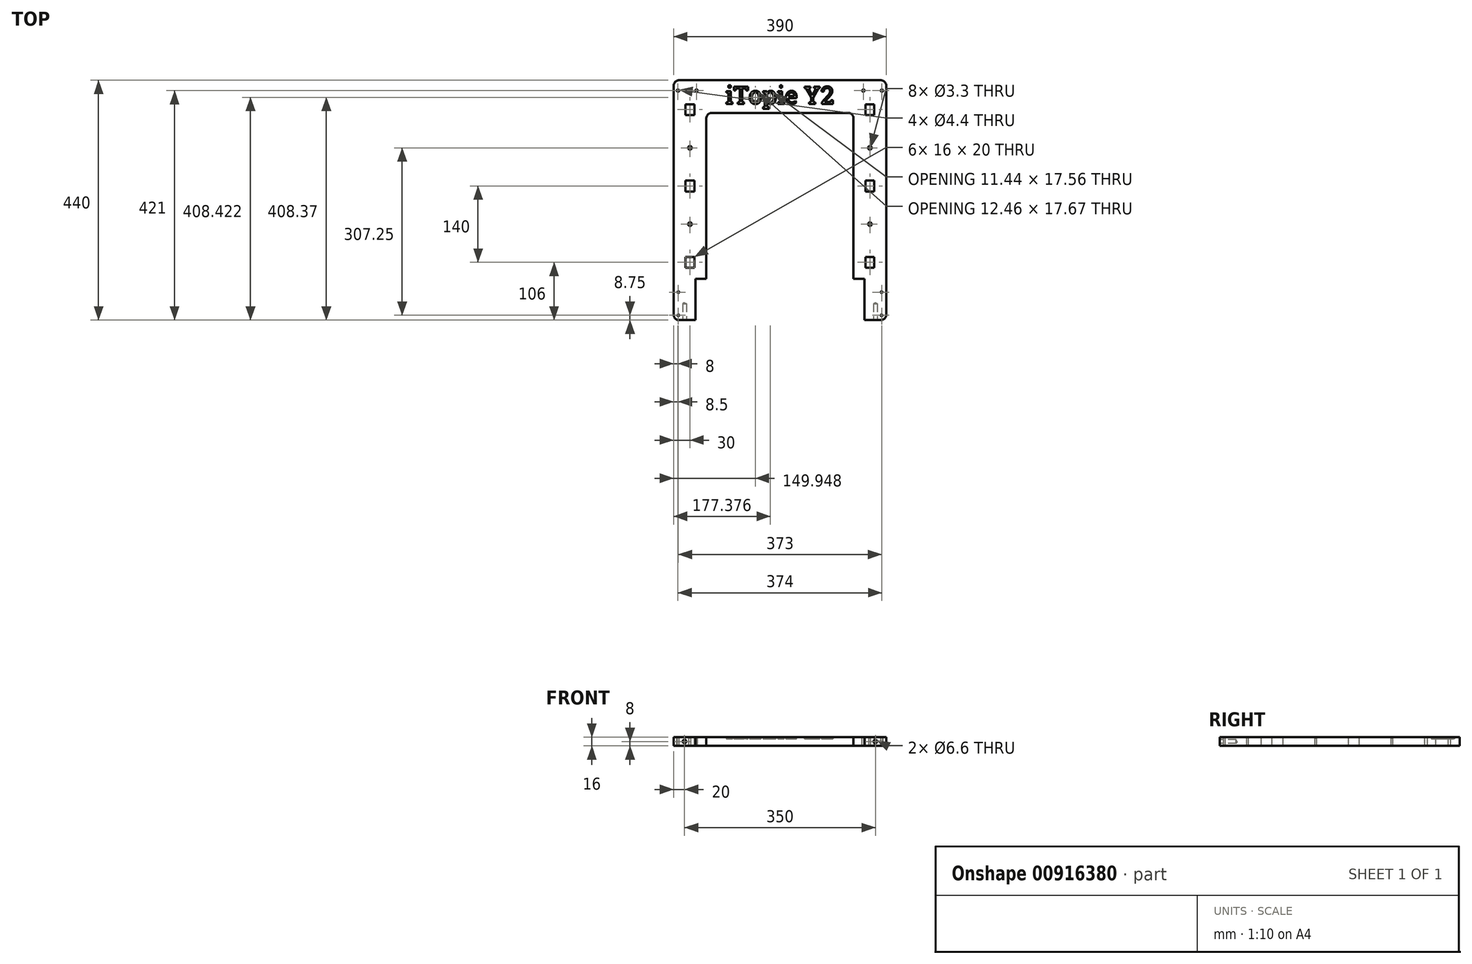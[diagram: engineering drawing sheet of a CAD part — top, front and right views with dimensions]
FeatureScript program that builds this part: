
annotation { "Feature Type Name" : "Feature", "Feature Type Description" : "" }
export const myFeature = defineFeature(function(context is Context, id is Id, definition is map)
    precondition{}
    {
        {
            var Q0;
            Q0=qCreatedBy(makeId("Top.planeOp"),FACE);
            var sketch = newSketch(context, id + "F0", { "sketchPlane" : qUnion([Q0])});
            skLineSegment(sketch, "E0.bottom", {"start": v(195, 220) * mm, "end": v(-195, 220) * mm});
            skLineSegment(sketch, "E0.top", {"start": v(195, -220) * mm, "end": v(-195, -220) * mm});
            skLineSegment(sketch, "E0.left", {"start": v(195, 220) * mm, "end": v(195, -220) * mm});
            skLineSegment(sketch, "E0.right", {"start": v(-195, 220) * mm, "end": v(-195, -220) * mm});
            skPoint(sketch, "E0.middle", {"position": v(0, 0) * mm});
            skLineSegment(sketch, "E1", {"start": v(-135, -220) * mm, "end": v(-135, 160) * mm});
            skLineSegment(sketch, "E2", {"start": v(-135, 160) * mm, "end": v(135, 160) * mm});
            skLineSegment(sketch, "E3", {"start": v(135, 160) * mm, "end": v(135, -220) * mm});
            skLineSegment(sketch, "E4", {"start": v(0, 0) * mm, "end": v(0, 160) * mm, "construction": true});
            skSolve(sketch);
        }
        {
            var Q0;
            Q0=makeQuery(id+"F0.imprint","IMPRINT",FACE,{"disambiguationData":[TD([[makeQuery(id+"F0.imprint","IMPRINT",EDGE,{"derivedFrom":sQuery(id+"F0.wireOp",EDGE,"E0.bottom")}),1.0]])]});
            extrude(context, id + "F1", {"entities" : qUnion([Q0]), "depth" : 16 * mm});
        }
        {
            var Q0;
            Q0=makeQuery(id+"F1.opExtrude","CAP_FACE",FACE,{"disambiguationData":[OSD([sQuery(id+"F0.wireOp",EDGE,"E0.bottom"),sQuery(id+"F0.wireOp",EDGE,"E0.top"),sQuery(id+"F0.wireOp",EDGE,"E0.left"),sQuery(id+"F0.wireOp",EDGE,"E0.right"),sQuery(id+"F0.wireOp",EDGE,"E1"),sQuery(id+"F0.wireOp",EDGE,"E2"),sQuery(id+"F0.wireOp",EDGE,"E3")])],"isStart":false});
            var sketch = newSketch(context, id + "F2", { "sketchPlane" : qUnion([Q0])});
            skLineSegment(sketch, "E5", {"start": v(-165, 166) * mm, "end": v(-165, 26) * mm, "construction": true});
            skLineSegment(sketch, "E6", {"start": v(-165, 26) * mm, "end": v(-165, -114) * mm, "construction": true});
            skLineSegment(sketch, "E7.bottom", {"start": v(-157, 176) * mm, "end": v(-173, 176) * mm});
            skLineSegment(sketch, "E7.top", {"start": v(-157, 156) * mm, "end": v(-173, 156) * mm});
            skLineSegment(sketch, "E7.left", {"start": v(-157, 176) * mm, "end": v(-157, 156) * mm});
            skLineSegment(sketch, "E7.right", {"start": v(-173, 176) * mm, "end": v(-173, 156) * mm});
            skPoint(sketch, "E7.middle", {"position": v(-165, 166) * mm});
            skLineSegment(sketch, "E8.bottom", {"start": v(-157, 36) * mm, "end": v(-173, 36) * mm});
            skLineSegment(sketch, "E8.top", {"start": v(-157, 16) * mm, "end": v(-173, 16) * mm});
            skLineSegment(sketch, "E8.left", {"start": v(-157, 36) * mm, "end": v(-157, 16) * mm});
            skLineSegment(sketch, "E8.right", {"start": v(-173, 36) * mm, "end": v(-173, 16) * mm});
            skPoint(sketch, "E8.middle", {"position": v(-165, 26) * mm});
            skLineSegment(sketch, "E9.bottom", {"start": v(-157, -104) * mm, "end": v(-173, -104) * mm});
            skLineSegment(sketch, "E9.top", {"start": v(-157, -124) * mm, "end": v(-173, -124) * mm});
            skLineSegment(sketch, "E9.left", {"start": v(-157, -104) * mm, "end": v(-157, -124) * mm});
            skLineSegment(sketch, "E9.right", {"start": v(-173, -104) * mm, "end": v(-173, -124) * mm});
            skPoint(sketch, "E9.middle", {"position": v(-165, -114) * mm});
            skLineSegment(sketch, "E10.MirrorCS", {"start": v(157, 36) * mm, "end": v(173, 36) * mm});
            skLineSegment(sketch, "E11.MirrorCS", {"start": v(173, 176) * mm, "end": v(173, 156) * mm});
            skLineSegment(sketch, "E12.MirrorCS", {"start": v(157, 156) * mm, "end": v(173, 156) * mm});
            skLineSegment(sketch, "E13.MirrorCS", {"start": v(157, 176) * mm, "end": v(173, 176) * mm});
            skLineSegment(sketch, "E14.MirrorCS", {"start": v(157, 16) * mm, "end": v(173, 16) * mm});
            skLineSegment(sketch, "E15.MirrorCS", {"start": v(157, 36) * mm, "end": v(157, 16) * mm});
            skLineSegment(sketch, "E16.MirrorCS", {"start": v(173, 36) * mm, "end": v(173, 16) * mm});
            skLineSegment(sketch, "E17.MirrorCS", {"start": v(157, -104) * mm, "end": v(173, -104) * mm});
            skLineSegment(sketch, "E18.MirrorCS", {"start": v(157, -124) * mm, "end": v(173, -124) * mm});
            skLineSegment(sketch, "E19.MirrorCS", {"start": v(173, -104) * mm, "end": v(173, -124) * mm});
            skLineSegment(sketch, "E20.MirrorCS", {"start": v(157, -104) * mm, "end": v(157, -124) * mm});
            skLineSegment(sketch, "E21.MirrorCS", {"start": v(157, 176) * mm, "end": v(157, 156) * mm});
            skLineSegment(sketch, "E22.MirrorCS", {"start": v(165, 166) * mm, "end": v(165, 26) * mm, "construction": true});
            skLineSegment(sketch, "E23.MirrorCS", {"start": v(165, 26) * mm, "end": v(165, -114) * mm, "construction": true});
            skPoint(sketch, "E24.MirrorP", {"position": v(165, 26) * mm});
            skPoint(sketch, "E25.MirrorP", {"position": v(165, 166) * mm});
            skPoint(sketch, "E26.MirrorP", {"position": v(165, -114) * mm});
            skLineSegment(sketch, "E27.bottom", {"start": v(-135, -220) * mm, "end": v(-155, -220) * mm});
            skLineSegment(sketch, "E27.top", {"start": v(-135, -144) * mm, "end": v(-155, -144) * mm});
            skLineSegment(sketch, "E27.left", {"start": v(-135, -220) * mm, "end": v(-135, -144) * mm});
            skLineSegment(sketch, "E27.right", {"start": v(-155, -220) * mm, "end": v(-155, -144) * mm});
            skLineSegment(sketch, "E28.MirrorCS", {"start": v(135, -144) * mm, "end": v(155, -144) * mm});
            skLineSegment(sketch, "E29.MirrorCS", {"start": v(135, -220) * mm, "end": v(155, -220) * mm});
            skLineSegment(sketch, "E30.MirrorCS", {"start": v(155, -220) * mm, "end": v(155, -144) * mm});
            skLineSegment(sketch, "E31.MirrorCS", {"start": v(135, -220) * mm, "end": v(135, -144) * mm});
            skSolve(sketch);
        }
        {
            var Q0;
            Q0=makeQuery(id+"F2.imprint","IMPRINT",FACE,{"disambiguationData":[TD([[makeQuery(id+"F2.imprint","IMPRINT",EDGE,{"derivedFrom":sQuery(id+"F2.wireOp",EDGE,"E27.bottom")}),-1.0]])]});
            var Q1;
            Q1=makeQuery(id+"F2.imprint","IMPRINT",FACE,{"disambiguationData":[TD([[makeQuery(id+"F2.imprint","IMPRINT",EDGE,{"derivedFrom":sQuery(id+"F2.wireOp",EDGE,"E7.bottom")}),1.0]])]});
            var Q2;
            Q2=makeQuery(id+"F2.imprint","IMPRINT",FACE,{"disambiguationData":[TD([[makeQuery(id+"F2.imprint","IMPRINT",EDGE,{"derivedFrom":sQuery(id+"F2.wireOp",EDGE,"E9.bottom")}),1.0]])]});
            var Q3;
            Q3=makeQuery(id+"F2.imprint","IMPRINT",FACE,{"disambiguationData":[TD([[makeQuery(id+"F2.imprint","IMPRINT",EDGE,{"derivedFrom":sQuery(id+"F2.wireOp",EDGE,"E8.bottom")}),1.0]])]});
            var Q4;
            Q4=makeQuery(id+"F2.imprint","IMPRINT",FACE,{"disambiguationData":[TD([[makeQuery(id+"F2.imprint","IMPRINT",EDGE,{"derivedFrom":sQuery(id+"F2.wireOp",EDGE,"E28.MirrorCS")}),-1.0]])]});
            var Q5;
            Q5=makeQuery(id+"F2.imprint","IMPRINT",FACE,{"disambiguationData":[TD([[makeQuery(id+"F2.imprint","IMPRINT",EDGE,{"derivedFrom":sQuery(id+"F2.wireOp",EDGE,"E10.MirrorCS")}),-1.0]])]});
            var Q6;
            Q6=makeQuery(id+"F2.imprint","IMPRINT",FACE,{"disambiguationData":[TD([[makeQuery(id+"F2.imprint","IMPRINT",EDGE,{"derivedFrom":sQuery(id+"F2.wireOp",EDGE,"E11.MirrorCS")}),-1.0]])]});
            var Q7;
            Q7=makeQuery(id+"F2.imprint","IMPRINT",FACE,{"disambiguationData":[TD([[makeQuery(id+"F2.imprint","IMPRINT",EDGE,{"derivedFrom":sQuery(id+"F2.wireOp",EDGE,"E17.MirrorCS")}),-1.0]])]});
            extrude(context, id + "F3", {"entities" : qUnion([Q0, Q1, Q2, Q3, Q4, Q5, Q6, Q7]), "operationType" : NewBodyOperationType.REMOVE, "endBound" : BoundingType.UP_TO_NEXT, "oppositeDirection" : true, "depth" : 25 * mm});
        }
        {
            var Q0;
            Q0=makeQuery(id+"F1.opExtrude","SWEPT_EDGE",EDGE,{"disambiguationData":[OSD([sQuery(id+"F0.wireOp",EDGE,"E1"),sQuery(id+"F0.wireOp",EDGE,"E2")])]});
            var Q1;
            Q1=makeQuery(id+"F1.opExtrude","SWEPT_EDGE",EDGE,{"disambiguationData":[OSD([sQuery(id+"F0.wireOp",EDGE,"E2"),sQuery(id+"F0.wireOp",EDGE,"E3")])]});
            var Q2;
            Q2=makeQuery(id+"F1.opExtrude","SWEPT_EDGE",EDGE,{"disambiguationData":[OSD([sQuery(id+"F0.wireOp",EDGE,"E0.bottom"),sQuery(id+"F0.wireOp",EDGE,"E0.right")])]});
            var Q3;
            Q3=makeQuery(id+"F1.opExtrude","SWEPT_EDGE",EDGE,{"disambiguationData":[OSD([sQuery(id+"F0.wireOp",EDGE,"E0.bottom"),sQuery(id+"F0.wireOp",EDGE,"E0.left")])]});
            var Q4;
            Q4=makeQuery(id+"F1.opExtrude","SWEPT_EDGE",EDGE,{"disambiguationData":[OSD([sQuery(id+"F0.wireOp",EDGE,"E0.top"),sQuery(id+"F0.wireOp",EDGE,"E0.left")])]});
            var Q5;
            Q5=makeQuery(id+"F3.boolean.opBoolean","COPY",EDGE,{"derivedFrom":makeQuery(id+"F3.opExtrude","SWEPT_EDGE",EDGE,{"disambiguationData":[OSD([sQuery(id+"F0.wireOp",EDGE,"E0.top"),sQuery(id+"F2.wireOp",EDGE,"E29.MirrorCS"),sQuery(id+"F2.wireOp",EDGE,"E30.MirrorCS")])]})});
            var Q6;
            Q6=makeQuery(id+"F3.boolean.opBoolean","COPY",EDGE,{"derivedFrom":makeQuery(id+"F3.opExtrude","SWEPT_EDGE",EDGE,{"disambiguationData":[OSD([sQuery(id+"F0.wireOp",EDGE,"E0.top"),sQuery(id+"F2.wireOp",EDGE,"E27.bottom"),sQuery(id+"F2.wireOp",EDGE,"E27.right")])]})});
            var Q7;
            Q7=makeQuery(id+"F1.opExtrude","SWEPT_EDGE",EDGE,{"disambiguationData":[OSD([sQuery(id+"F0.wireOp",EDGE,"E0.top"),sQuery(id+"F0.wireOp",EDGE,"E0.right")])]});
            fillet(context, id + "F4", {"entities" : qUnion([Q0, Q1, Q2, Q3, Q4, Q5, Q6, Q7]), "radius" : 10 * mm, "tangentPropagation" : true, "allowEdgeOverflow" : false});
        }
        {
            var Q0;
            Q0=makeQuery(id+"F1.opExtrude","CAP_FACE",FACE,{"disambiguationData":[OSD([sQuery(id+"F0.wireOp",EDGE,"E0.bottom"),sQuery(id+"F0.wireOp",EDGE,"E0.top"),sQuery(id+"F0.wireOp",EDGE,"E0.left"),sQuery(id+"F0.wireOp",EDGE,"E0.right"),sQuery(id+"F0.wireOp",EDGE,"E1"),sQuery(id+"F0.wireOp",EDGE,"E2"),sQuery(id+"F0.wireOp",EDGE,"E3")])],"isStart":false});
            var sketch = newSketch(context, id + "F5", { "sketchPlane" : qUnion([Q0])});
            skLineSegment(sketch, "E32", {"start": v(-165, 36) * mm, "end": v(-165, 96) * mm});
            skLineSegment(sketch, "E33", {"start": v(-165, 16) * mm, "end": v(-165, -44) * mm});
            skLineSegment(sketch, "E34", {"start": v(165, 36) * mm, "end": v(165, 96) * mm});
            skLineSegment(sketch, "E35", {"start": v(165, 16) * mm, "end": v(165, -44) * mm});
            skSolve(sketch);
        }
        {
            var Q0;
            Q0=sQuery(id+"F5.wireOp",VERTEX,"E32.end");
            var Q1;
            Q1=sQuery(id+"F5.wireOp",VERTEX,"E33.end");
            var Q2;
            Q2=sQuery(id+"F5.wireOp",VERTEX,"E34.end");
            var Q3;
            Q3=sQuery(id+"F5.wireOp",VERTEX,"E35.end");
            var Q4;
            Q4=makeQuery(id+"F1.opExtrude","SWEPT_BODY",BODY,{"disambiguationData":[OSD([sQuery(id+"F0.wireOp",EDGE,"E0.bottom"),sQuery(id+"F0.wireOp",EDGE,"E0.top"),sQuery(id+"F0.wireOp",EDGE,"E0.left"),sQuery(id+"F0.wireOp",EDGE,"E0.right"),sQuery(id+"F0.wireOp",EDGE,"E1"),sQuery(id+"F0.wireOp",EDGE,"E2"),sQuery(id+"F0.wireOp",EDGE,"E3")])]});
            hole(context, id + "F6", {"style" : HoleStyle.C_SINK, "endStyle" : HoleEndStyle.THROUGH, "standardTappedOrClearance" : lookupTablePath({ "standard" : "ISO", "fit" : "Normal", "size" : "M3", "type" : "Clearance" }), "standardBlindInLast" : lookupTablePath({ "fit" : "Standard", "standard" : "ISO", "size" : "M3", "type" : "Clearance" }), "holeDiameter" : 3.3 * mm, "cSinkDiameter" : 6.72 * mm, "cSinkAngle" : 90 * degree, "tappedDepth" : 12 * mm, "tapClearance" : 3, "locations" : qUnion([Q0, Q1, Q2, Q3]), "scope" : qUnion([Q4])});
        }
        {
            var Q0;
            {var subQ0=sQuery(id+"F0.wireOp",EDGE,"E0.top");Q0=makeQuery(id+"F1.opExtrude","SWEPT_FACE",FACE,{"disambiguationData":[OSD([subQ0]),TDD([makeQuery(id+"F0.imprint","IMPRINT",EDGE,{"disambiguationData":[TD([[makeQuery(id+"F0.imprint","INTERSECT",VERTEX,{"derivedFrom":[subQ0,sQuery(id+"F0.wireOp",EDGE,"E0.right")]}),1.0]])],"derivedFrom":subQ0})])]});}
            var sketch = newSketch(context, id + "F7", { "sketchPlane" : qUnion([Q0])});
            skLineSegment(sketch, "E36", {"start": v(-165, 0) * mm, "end": v(-175, 8) * mm});
            skLineSegment(sketch, "E37", {"start": v(-175, 8) * mm, "end": v(-185, 16) * mm});
            skLineSegment(sketch, "E38.0.0", {"start": v(185, 16) * mm, "end": v(165, 16) * mm});
            skLineSegment(sketch, "E38.0.1", {"start": v(165, 16) * mm, "end": v(165, 0) * mm});
            skLineSegment(sketch, "E38.0.2", {"start": v(165, 0) * mm, "end": v(185, 0) * mm});
            skLineSegment(sketch, "E38.0.3", {"start": v(185, 0) * mm, "end": v(185, 16) * mm});
            skLineSegment(sketch, "E39", {"start": v(185, 0) * mm, "end": v(175, 8) * mm});
            skPoint(sketch, "E39.endSnap0", {"position": v(165, 8) * mm});
            skPoint(sketch, "E39.endSnap1", {"position": v(175, 16) * mm});
            skLineSegment(sketch, "E40", {"start": v(175, 8) * mm, "end": v(165, 16) * mm});
            skSolve(sketch);
        }
        {
            var Q0;
            Q0=sQuery(id+"F7.wireOp",VERTEX,"E37.start");
            var Q1;
            Q1=sQuery(id+"F7.wireOp",VERTEX,"E40.start");
            var Q2;
            Q2=makeQuery(id+"F1.opExtrude","SWEPT_BODY",BODY,{"disambiguationData":[OSD([sQuery(id+"F0.wireOp",EDGE,"E0.bottom"),sQuery(id+"F0.wireOp",EDGE,"E0.top"),sQuery(id+"F0.wireOp",EDGE,"E0.left"),sQuery(id+"F0.wireOp",EDGE,"E0.right"),sQuery(id+"F0.wireOp",EDGE,"E1"),sQuery(id+"F0.wireOp",EDGE,"E2"),sQuery(id+"F0.wireOp",EDGE,"E3")])]});
            hole(context, id + "F8", {"style" : HoleStyle.SIMPLE, "endStyle" : HoleEndStyle.BLIND, "standardTappedOrClearance" : lookupTablePath({ "standard" : "ISO", "fit" : "Normal", "size" : "M6", "type" : "Clearance" }), "standardBlindInLast" : lookupTablePath({ "fit" : "Standard", "standard" : "ISO", "size" : "M6", "type" : "Clearance" }), "holeDiameter" : 6.6 * mm, "holeDepth" : 30 * mm, "tappedDepth" : 12 * mm, "tapClearance" : 3, "locations" : qUnion([Q0, Q1]), "scope" : qUnion([Q2])});
        }
        {
            var Q0;
            Q0=makeQuery(id+"F1.opExtrude","CAP_FACE",FACE,{"disambiguationData":[OSD([sQuery(id+"F0.wireOp",EDGE,"E0.bottom"),sQuery(id+"F0.wireOp",EDGE,"E0.top"),sQuery(id+"F0.wireOp",EDGE,"E0.left"),sQuery(id+"F0.wireOp",EDGE,"E0.right"),sQuery(id+"F0.wireOp",EDGE,"E1"),sQuery(id+"F0.wireOp",EDGE,"E2"),sQuery(id+"F0.wireOp",EDGE,"E3")])],"isStart":false});
            var sketch = newSketch(context, id + "F9", { "sketchPlane" : qUnion([Q0])});
            skLineSegment(sketch, "E41", {"start": v(-195, 201) * mm, "end": v(-187, 201) * mm});
            skLineSegment(sketch, "E42", {"start": v(-187, 201) * mm, "end": v(-153, 201) * mm});
            skLineSegment(sketch, "E43.MirrorCS", {"start": v(195, 201) * mm, "end": v(187, 201) * mm});
            skLineSegment(sketch, "E44.MirrorCS", {"start": v(187, 201) * mm, "end": v(153, 201) * mm});
            skSolve(sketch);
        }
        {
            var Q0;
            Q0=sQuery(id+"F9.wireOp",VERTEX,"E42.start");
            var Q1;
            Q1=sQuery(id+"F9.wireOp",VERTEX,"E42.end");
            var Q2;
            Q2=sQuery(id+"F9.wireOp",VERTEX,"E44.MirrorCS.start");
            var Q3;
            Q3=sQuery(id+"F9.wireOp",VERTEX,"E44.MirrorCS.end");
            var Q4;
            Q4=makeQuery(id+"F1.opExtrude","SWEPT_BODY",BODY,{"disambiguationData":[OSD([sQuery(id+"F0.wireOp",EDGE,"E0.bottom"),sQuery(id+"F0.wireOp",EDGE,"E0.top"),sQuery(id+"F0.wireOp",EDGE,"E0.left"),sQuery(id+"F0.wireOp",EDGE,"E0.right"),sQuery(id+"F0.wireOp",EDGE,"E1"),sQuery(id+"F0.wireOp",EDGE,"E2"),sQuery(id+"F0.wireOp",EDGE,"E3")])]});
            hole(context, id + "F10", {"style" : HoleStyle.SIMPLE, "endStyle" : HoleEndStyle.THROUGH, "standardTappedOrClearance" : lookupTablePath({ "standard" : "ISO", "fit" : "Normal", "size" : "M4", "type" : "Clearance" }), "standardBlindInLast" : lookupTablePath({ "fit" : "Standard", "standard" : "ISO", "size" : "M4", "type" : "Clearance" }), "holeDiameter" : 4.4 * mm, "tappedDepth" : 12 * mm, "tapClearance" : 3, "locations" : qUnion([Q0, Q1, Q2, Q3]), "scope" : qUnion([Q4])});
        }
        {
            var Q0;
            Q0=makeQuery(id+"F1.opExtrude","CAP_FACE",FACE,{"disambiguationData":[OSD([sQuery(id+"F0.wireOp",EDGE,"E0.bottom"),sQuery(id+"F0.wireOp",EDGE,"E0.top"),sQuery(id+"F0.wireOp",EDGE,"E0.left"),sQuery(id+"F0.wireOp",EDGE,"E0.right"),sQuery(id+"F0.wireOp",EDGE,"E1"),sQuery(id+"F0.wireOp",EDGE,"E2"),sQuery(id+"F0.wireOp",EDGE,"E3")])],"isStart":false});
            var sketch = newSketch(context, id + "F11", { "sketchPlane" : qUnion([Q0])});
            skLineSegment(sketch, "E45", {"start": v(-186.5, -220) * mm, "end": v(-186.5, -211.25) * mm});
            skLineSegment(sketch, "E46", {"start": v(-186.5, -211.25) * mm, "end": v(-186.5, -168.75) * mm});
            skLineSegment(sketch, "E47.MirrorCS", {"start": v(186.5, -220) * mm, "end": v(186.5, -211.25) * mm});
            skLineSegment(sketch, "E48.MirrorCS", {"start": v(186.5, -211.25) * mm, "end": v(186.5, -168.75) * mm});
            skSolve(sketch);
        }
        {
            var Q0;
            Q0=sQuery(id+"F11.wireOp",VERTEX,"E46.end");
            var Q1;
            Q1=sQuery(id+"F11.wireOp",VERTEX,"E46.start");
            var Q2;
            Q2=sQuery(id+"F11.wireOp",VERTEX,"E48.MirrorCS.start");
            var Q3;
            Q3=sQuery(id+"F11.wireOp",VERTEX,"E48.MirrorCS.end");
            var Q4;
            Q4=makeQuery(id+"F1.opExtrude","SWEPT_BODY",BODY,{"disambiguationData":[OSD([sQuery(id+"F0.wireOp",EDGE,"E0.bottom"),sQuery(id+"F0.wireOp",EDGE,"E0.top"),sQuery(id+"F0.wireOp",EDGE,"E0.left"),sQuery(id+"F0.wireOp",EDGE,"E0.right"),sQuery(id+"F0.wireOp",EDGE,"E1"),sQuery(id+"F0.wireOp",EDGE,"E2"),sQuery(id+"F0.wireOp",EDGE,"E3")])]});
            hole(context, id + "F12", {"style" : HoleStyle.SIMPLE, "endStyle" : HoleEndStyle.THROUGH, "standardTappedOrClearance" : lookupTablePath({ "standard" : "ISO", "fit" : "Normal", "size" : "M3", "type" : "Clearance" }), "standardBlindInLast" : lookupTablePath({ "fit" : "Standard", "standard" : "ISO", "size" : "M3", "type" : "Clearance" }), "holeDiameter" : 3.3 * mm, "tappedDepth" : 12 * mm, "tapClearance" : 3, "locations" : qUnion([Q0, Q1, Q2, Q3]), "scope" : qUnion([Q4])});
        }
        {
            var Q0;
            Q0=makeQuery(id+"F1.opExtrude","CAP_FACE",FACE,{"disambiguationData":[OSD([sQuery(id+"F0.wireOp",EDGE,"E0.bottom"),sQuery(id+"F0.wireOp",EDGE,"E0.top"),sQuery(id+"F0.wireOp",EDGE,"E0.left"),sQuery(id+"F0.wireOp",EDGE,"E0.right"),sQuery(id+"F0.wireOp",EDGE,"E1"),sQuery(id+"F0.wireOp",EDGE,"E2"),sQuery(id+"F0.wireOp",EDGE,"E3")])],"isStart":false});
            var sketch = newSketch(context, id + "F13", { "sketchPlane" : qUnion([Q0])});
            skText(sketch, "E49", { "text": "iTopie Y2", "fontName": "RobotoSlab-Regular.ttf"});
            const initialGuessF13  = {"E49": [-0.1, 0.1767, 1, 0, 0.03201]};
            skSetInitialGuess(sketch, initialGuessF13);
            skSolve(sketch);
        }
        {
            var Q0;
            Q0=makeQuery(id+"F13.imprint","IMPRINT",FACE,{"disambiguationData":[TD([[makeQuery(id+"F13.imprint","IMPRINT",EDGE,{"derivedFrom":sQuery(id+"F13.wireOp",EDGE,"E49.sketch_text.stroke-30")}),-1.0]])]});
            var Q1;
            Q1=makeQuery(id+"F13.imprint","IMPRINT",FACE,{"disambiguationData":[TD([[makeQuery(id+"F13.imprint","IMPRINT",EDGE,{"derivedFrom":sQuery(id+"F13.wireOp",EDGE,"E49.sketch_text.stroke-14")}),-1.0]])]});
            var Q2;
            Q2=makeQuery(id+"F13.imprint","IMPRINT",FACE,{"disambiguationData":[TD([[makeQuery(id+"F13.imprint","IMPRINT",EDGE,{"derivedFrom":sQuery(id+"F13.wireOp",EDGE,"E49.sketch_text.stroke-10")}),-1.0]])]});
            var Q3;
            Q3=makeQuery(id+"F13.imprint","IMPRINT",FACE,{"disambiguationData":[TD([[makeQuery(id+"F13.imprint","IMPRINT",EDGE,{"derivedFrom":sQuery(id+"F13.wireOp",EDGE,"E49.sketch_text.stroke-0")}),-1.0]])]});
            var Q4;
            Q4=makeQuery(id+"F13.imprint","IMPRINT",FACE,{"disambiguationData":[TD([[makeQuery(id+"F13.imprint","IMPRINT",EDGE,{"derivedFrom":sQuery(id+"F13.wireOp",EDGE,"E49.sketch_text.stroke-50")}),-1.0]])]});
            var Q5;
            Q5=makeQuery(id+"F13.imprint","IMPRINT",FACE,{"disambiguationData":[TD([[makeQuery(id+"F13.imprint","IMPRINT",EDGE,{"derivedFrom":sQuery(id+"F13.wireOp",EDGE,"E49.sketch_text.stroke-80")}),-1.0]])]});
            var Q6;
            Q6=makeQuery(id+"F13.imprint","IMPRINT",FACE,{"disambiguationData":[TD([[makeQuery(id+"F13.imprint","IMPRINT",EDGE,{"derivedFrom":sQuery(id+"F13.wireOp",EDGE,"E49.sketch_text.stroke-90")}),-1.0]])]});
            var Q7;
            Q7=makeQuery(id+"F13.imprint","IMPRINT",FACE,{"disambiguationData":[TD([[makeQuery(id+"F13.imprint","IMPRINT",EDGE,{"derivedFrom":sQuery(id+"F13.wireOp",EDGE,"E49.sketch_text.stroke-94")}),-1.0]])]});
            var Q8;
            Q8=makeQuery(id+"F13.imprint","IMPRINT",FACE,{"disambiguationData":[TD([[makeQuery(id+"F13.imprint","IMPRINT",EDGE,{"derivedFrom":sQuery(id+"F13.wireOp",EDGE,"E49.sketch_text.stroke-118")}),-1.0]])]});
            var Q9;
            Q9=makeQuery(id+"F13.imprint","IMPRINT",FACE,{"disambiguationData":[TD([[makeQuery(id+"F13.imprint","IMPRINT",EDGE,{"derivedFrom":sQuery(id+"F13.wireOp",EDGE,"E49.sketch_text.stroke-139")}),-1.0]])]});
            extrude(context, id + "F14", {"entities" : qUnion([Q0, Q1, Q2, Q3, Q4, Q5, Q6, Q7, Q8, Q9]), "operationType" : NewBodyOperationType.REMOVE, "oppositeDirection" : true, "depth" : 3 * mm, "offsetDistance" : 25 * mm});
        }
        {
            var Q0;
            Q0=makeQuery(id+"F14.boolean.opBoolean","COPY",FACE,{"derivedFrom":makeQuery(id+"F14.opExtrude","CAP_FACE",FACE,{"disambiguationData":[OSD([sQuery(id+"F13.wireOp",EDGE,"E49.sketch_text.stroke-139"),sQuery(id+"F13.wireOp",EDGE,"E49.sketch_text.stroke-140"),sQuery(id+"F13.wireOp",EDGE,"E49.sketch_text.stroke-141"),sQuery(id+"F13.wireOp",EDGE,"E49.sketch_text.stroke-142"),sQuery(id+"F13.wireOp",EDGE,"E49.sketch_text.stroke-143"),sQuery(id+"F13.wireOp",EDGE,"E49.sketch_text.stroke-144"),sQuery(id+"F13.wireOp",EDGE,"E49.sketch_text.stroke-145"),sQuery(id+"F13.wireOp",EDGE,"E49.sketch_text.stroke-146"),sQuery(id+"F13.wireOp",EDGE,"E49.sketch_text.stroke-147"),sQuery(id+"F13.wireOp",EDGE,"E49.sketch_text.stroke-148"),sQuery(id+"F13.wireOp",EDGE,"E49.sketch_text.stroke-149"),sQuery(id+"F13.wireOp",EDGE,"E49.sketch_text.stroke-150"),sQuery(id+"F13.wireOp",EDGE,"E49.sketch_text.stroke-151"),sQuery(id+"F13.wireOp",EDGE,"E49.sketch_text.stroke-152"),sQuery(id+"F13.wireOp",EDGE,"E49.sketch_text.stroke-153"),sQuery(id+"F13.wireOp",EDGE,"E49.sketch_text.stroke-154"),sQuery(id+"F13.wireOp",EDGE,"E49.sketch_text.stroke-155"),sQuery(id+"F13.wireOp",EDGE,"E49.sketch_text.stroke-156"),sQuery(id+"F13.wireOp",EDGE,"E49.sketch_text.stroke-157"),sQuery(id+"F13.wireOp",EDGE,"E49.sketch_text.stroke-158"),sQuery(id+"F13.wireOp",EDGE,"E49.sketch_text.stroke-159"),sQuery(id+"F13.wireOp",EDGE,"E49.sketch_text.stroke-160"),sQuery(id+"F13.wireOp",EDGE,"E49.sketch_text.stroke-161")])],"isStart":false})});
            var Q1;
            Q1=makeQuery(id+"F14.boolean.opBoolean","COPY",FACE,{"derivedFrom":makeQuery(id+"F14.opExtrude","CAP_FACE",FACE,{"disambiguationData":[OSD([sQuery(id+"F13.wireOp",EDGE,"E49.sketch_text.stroke-118"),sQuery(id+"F13.wireOp",EDGE,"E49.sketch_text.stroke-119"),sQuery(id+"F13.wireOp",EDGE,"E49.sketch_text.stroke-120"),sQuery(id+"F13.wireOp",EDGE,"E49.sketch_text.stroke-121"),sQuery(id+"F13.wireOp",EDGE,"E49.sketch_text.stroke-122"),sQuery(id+"F13.wireOp",EDGE,"E49.sketch_text.stroke-123"),sQuery(id+"F13.wireOp",EDGE,"E49.sketch_text.stroke-124"),sQuery(id+"F13.wireOp",EDGE,"E49.sketch_text.stroke-125"),sQuery(id+"F13.wireOp",EDGE,"E49.sketch_text.stroke-126"),sQuery(id+"F13.wireOp",EDGE,"E49.sketch_text.stroke-127"),sQuery(id+"F13.wireOp",EDGE,"E49.sketch_text.stroke-128"),sQuery(id+"F13.wireOp",EDGE,"E49.sketch_text.stroke-129"),sQuery(id+"F13.wireOp",EDGE,"E49.sketch_text.stroke-130"),sQuery(id+"F13.wireOp",EDGE,"E49.sketch_text.stroke-131"),sQuery(id+"F13.wireOp",EDGE,"E49.sketch_text.stroke-132"),sQuery(id+"F13.wireOp",EDGE,"E49.sketch_text.stroke-133"),sQuery(id+"F13.wireOp",EDGE,"E49.sketch_text.stroke-134"),sQuery(id+"F13.wireOp",EDGE,"E49.sketch_text.stroke-135"),sQuery(id+"F13.wireOp",EDGE,"E49.sketch_text.stroke-136"),sQuery(id+"F13.wireOp",EDGE,"E49.sketch_text.stroke-137"),sQuery(id+"F13.wireOp",EDGE,"E49.sketch_text.stroke-138")])],"isStart":false})});
            var Q2;
            Q2=makeQuery(id+"F14.boolean.opBoolean","COPY",FACE,{"derivedFrom":makeQuery(id+"F14.opExtrude","CAP_FACE",FACE,{"disambiguationData":[OSD([sQuery(id+"F13.wireOp",EDGE,"E49.sketch_text.stroke-94"),sQuery(id+"F13.wireOp",EDGE,"E49.sketch_text.stroke-95"),sQuery(id+"F13.wireOp",EDGE,"E49.sketch_text.stroke-96"),sQuery(id+"F13.wireOp",EDGE,"E49.sketch_text.stroke-97"),sQuery(id+"F13.wireOp",EDGE,"E49.sketch_text.stroke-98"),sQuery(id+"F13.wireOp",EDGE,"E49.sketch_text.stroke-99"),sQuery(id+"F13.wireOp",EDGE,"E49.sketch_text.stroke-100"),sQuery(id+"F13.wireOp",EDGE,"E49.sketch_text.stroke-101"),sQuery(id+"F13.wireOp",EDGE,"E49.sketch_text.stroke-102"),sQuery(id+"F13.wireOp",EDGE,"E49.sketch_text.stroke-103"),sQuery(id+"F13.wireOp",EDGE,"E49.sketch_text.stroke-104"),sQuery(id+"F13.wireOp",EDGE,"E49.sketch_text.stroke-105"),sQuery(id+"F13.wireOp",EDGE,"E49.sketch_text.stroke-106"),sQuery(id+"F13.wireOp",EDGE,"E49.sketch_text.stroke-107"),sQuery(id+"F13.wireOp",EDGE,"E49.sketch_text.stroke-108"),sQuery(id+"F13.wireOp",EDGE,"E49.sketch_text.stroke-109"),sQuery(id+"F13.wireOp",EDGE,"E49.sketch_text.stroke-110"),sQuery(id+"F13.wireOp",EDGE,"E49.sketch_text.stroke-111"),sQuery(id+"F13.wireOp",EDGE,"E49.sketch_text.stroke-112"),sQuery(id+"F13.wireOp",EDGE,"E49.sketch_text.stroke-113"),sQuery(id+"F13.wireOp",EDGE,"E49.sketch_text.stroke-114"),sQuery(id+"F13.wireOp",EDGE,"E49.sketch_text.stroke-115"),sQuery(id+"F13.wireOp",EDGE,"E49.sketch_text.stroke-116"),sQuery(id+"F13.wireOp",EDGE,"E49.sketch_text.stroke-117")])],"isStart":false})});
            var Q3;
            Q3=makeQuery(id+"F14.boolean.opBoolean","COPY",FACE,{"derivedFrom":makeQuery(id+"F14.opExtrude","CAP_FACE",FACE,{"disambiguationData":[OSD([sQuery(id+"F13.wireOp",EDGE,"E49.sketch_text.stroke-80"),sQuery(id+"F13.wireOp",EDGE,"E49.sketch_text.stroke-81"),sQuery(id+"F13.wireOp",EDGE,"E49.sketch_text.stroke-82"),sQuery(id+"F13.wireOp",EDGE,"E49.sketch_text.stroke-83"),sQuery(id+"F13.wireOp",EDGE,"E49.sketch_text.stroke-84"),sQuery(id+"F13.wireOp",EDGE,"E49.sketch_text.stroke-85"),sQuery(id+"F13.wireOp",EDGE,"E49.sketch_text.stroke-86"),sQuery(id+"F13.wireOp",EDGE,"E49.sketch_text.stroke-87"),sQuery(id+"F13.wireOp",EDGE,"E49.sketch_text.stroke-88"),sQuery(id+"F13.wireOp",EDGE,"E49.sketch_text.stroke-89")])],"isStart":false})});
            var Q4;
            Q4=makeQuery(id+"F14.boolean.opBoolean","COPY",FACE,{"derivedFrom":makeQuery(id+"F14.opExtrude","CAP_FACE",FACE,{"disambiguationData":[OSD([sQuery(id+"F13.wireOp",EDGE,"E49.sketch_text.stroke-50"),sQuery(id+"F13.wireOp",EDGE,"E49.sketch_text.stroke-51"),sQuery(id+"F13.wireOp",EDGE,"E49.sketch_text.stroke-52"),sQuery(id+"F13.wireOp",EDGE,"E49.sketch_text.stroke-53"),sQuery(id+"F13.wireOp",EDGE,"E49.sketch_text.stroke-54"),sQuery(id+"F13.wireOp",EDGE,"E49.sketch_text.stroke-55"),sQuery(id+"F13.wireOp",EDGE,"E49.sketch_text.stroke-56"),sQuery(id+"F13.wireOp",EDGE,"E49.sketch_text.stroke-57"),sQuery(id+"F13.wireOp",EDGE,"E49.sketch_text.stroke-58"),sQuery(id+"F13.wireOp",EDGE,"E49.sketch_text.stroke-59"),sQuery(id+"F13.wireOp",EDGE,"E49.sketch_text.stroke-60"),sQuery(id+"F13.wireOp",EDGE,"E49.sketch_text.stroke-61"),sQuery(id+"F13.wireOp",EDGE,"E49.sketch_text.stroke-62"),sQuery(id+"F13.wireOp",EDGE,"E49.sketch_text.stroke-63"),sQuery(id+"F13.wireOp",EDGE,"E49.sketch_text.stroke-64"),sQuery(id+"F13.wireOp",EDGE,"E49.sketch_text.stroke-65"),sQuery(id+"F13.wireOp",EDGE,"E49.sketch_text.stroke-66"),sQuery(id+"F13.wireOp",EDGE,"E49.sketch_text.stroke-67"),sQuery(id+"F13.wireOp",EDGE,"E49.sketch_text.stroke-68"),sQuery(id+"F13.wireOp",EDGE,"E49.sketch_text.stroke-69"),sQuery(id+"F13.wireOp",EDGE,"E49.sketch_text.stroke-70"),sQuery(id+"F13.wireOp",EDGE,"E49.sketch_text.stroke-71"),sQuery(id+"F13.wireOp",EDGE,"E49.sketch_text.stroke-72"),sQuery(id+"F13.wireOp",EDGE,"E49.sketch_text.stroke-73"),sQuery(id+"F13.wireOp",EDGE,"E49.sketch_text.stroke-74"),sQuery(id+"F13.wireOp",EDGE,"E49.sketch_text.stroke-75"),sQuery(id+"F13.wireOp",EDGE,"E49.sketch_text.stroke-76"),sQuery(id+"F13.wireOp",EDGE,"E49.sketch_text.stroke-77"),sQuery(id+"F13.wireOp",EDGE,"E49.sketch_text.stroke-78"),sQuery(id+"F13.wireOp",EDGE,"E49.sketch_text.stroke-79")])],"isStart":false})});
            var Q5;
            Q5=makeQuery(id+"F14.boolean.opBoolean","COPY",FACE,{"derivedFrom":makeQuery(id+"F14.opExtrude","CAP_FACE",FACE,{"disambiguationData":[OSD([sQuery(id+"F13.wireOp",EDGE,"E49.sketch_text.stroke-30"),sQuery(id+"F13.wireOp",EDGE,"E49.sketch_text.stroke-31"),sQuery(id+"F13.wireOp",EDGE,"E49.sketch_text.stroke-32"),sQuery(id+"F13.wireOp",EDGE,"E49.sketch_text.stroke-33"),sQuery(id+"F13.wireOp",EDGE,"E49.sketch_text.stroke-34"),sQuery(id+"F13.wireOp",EDGE,"E49.sketch_text.stroke-35"),sQuery(id+"F13.wireOp",EDGE,"E49.sketch_text.stroke-36"),sQuery(id+"F13.wireOp",EDGE,"E49.sketch_text.stroke-37"),sQuery(id+"F13.wireOp",EDGE,"E49.sketch_text.stroke-38"),sQuery(id+"F13.wireOp",EDGE,"E49.sketch_text.stroke-39"),sQuery(id+"F13.wireOp",EDGE,"E49.sketch_text.stroke-40"),sQuery(id+"F13.wireOp",EDGE,"E49.sketch_text.stroke-41"),sQuery(id+"F13.wireOp",EDGE,"E49.sketch_text.stroke-42"),sQuery(id+"F13.wireOp",EDGE,"E49.sketch_text.stroke-43"),sQuery(id+"F13.wireOp",EDGE,"E49.sketch_text.stroke-44"),sQuery(id+"F13.wireOp",EDGE,"E49.sketch_text.stroke-45"),sQuery(id+"F13.wireOp",EDGE,"E49.sketch_text.stroke-46"),sQuery(id+"F13.wireOp",EDGE,"E49.sketch_text.stroke-47"),sQuery(id+"F13.wireOp",EDGE,"E49.sketch_text.stroke-48"),sQuery(id+"F13.wireOp",EDGE,"E49.sketch_text.stroke-49")])],"isStart":false})});
            var Q6;
            Q6=makeQuery(id+"F14.boolean.opBoolean","COPY",FACE,{"derivedFrom":makeQuery(id+"F14.opExtrude","CAP_FACE",FACE,{"disambiguationData":[OSD([sQuery(id+"F13.wireOp",EDGE,"E49.sketch_text.stroke-14"),sQuery(id+"F13.wireOp",EDGE,"E49.sketch_text.stroke-15"),sQuery(id+"F13.wireOp",EDGE,"E49.sketch_text.stroke-16"),sQuery(id+"F13.wireOp",EDGE,"E49.sketch_text.stroke-17"),sQuery(id+"F13.wireOp",EDGE,"E49.sketch_text.stroke-18"),sQuery(id+"F13.wireOp",EDGE,"E49.sketch_text.stroke-19"),sQuery(id+"F13.wireOp",EDGE,"E49.sketch_text.stroke-20"),sQuery(id+"F13.wireOp",EDGE,"E49.sketch_text.stroke-21"),sQuery(id+"F13.wireOp",EDGE,"E49.sketch_text.stroke-22"),sQuery(id+"F13.wireOp",EDGE,"E49.sketch_text.stroke-23"),sQuery(id+"F13.wireOp",EDGE,"E49.sketch_text.stroke-24"),sQuery(id+"F13.wireOp",EDGE,"E49.sketch_text.stroke-25"),sQuery(id+"F13.wireOp",EDGE,"E49.sketch_text.stroke-26"),sQuery(id+"F13.wireOp",EDGE,"E49.sketch_text.stroke-27"),sQuery(id+"F13.wireOp",EDGE,"E49.sketch_text.stroke-28"),sQuery(id+"F13.wireOp",EDGE,"E49.sketch_text.stroke-29")])],"isStart":false})});
            var Q7;
            Q7=makeQuery(id+"F14.boolean.opBoolean","COPY",FACE,{"derivedFrom":makeQuery(id+"F14.opExtrude","CAP_FACE",FACE,{"disambiguationData":[OSD([sQuery(id+"F13.wireOp",EDGE,"E49.sketch_text.stroke-0"),sQuery(id+"F13.wireOp",EDGE,"E49.sketch_text.stroke-1"),sQuery(id+"F13.wireOp",EDGE,"E49.sketch_text.stroke-2"),sQuery(id+"F13.wireOp",EDGE,"E49.sketch_text.stroke-3"),sQuery(id+"F13.wireOp",EDGE,"E49.sketch_text.stroke-4"),sQuery(id+"F13.wireOp",EDGE,"E49.sketch_text.stroke-5"),sQuery(id+"F13.wireOp",EDGE,"E49.sketch_text.stroke-6"),sQuery(id+"F13.wireOp",EDGE,"E49.sketch_text.stroke-7"),sQuery(id+"F13.wireOp",EDGE,"E49.sketch_text.stroke-8"),sQuery(id+"F13.wireOp",EDGE,"E49.sketch_text.stroke-9")])],"isStart":false})});
            var Q8;
            Q8=makeQuery(id+"F14.boolean.opBoolean","COPY",FACE,{"derivedFrom":makeQuery(id+"F14.opExtrude","CAP_FACE",FACE,{"disambiguationData":[OSD([sQuery(id+"F13.wireOp",EDGE,"E49.sketch_text.stroke-10"),sQuery(id+"F13.wireOp",EDGE,"E49.sketch_text.stroke-11"),sQuery(id+"F13.wireOp",EDGE,"E49.sketch_text.stroke-12"),sQuery(id+"F13.wireOp",EDGE,"E49.sketch_text.stroke-13")])],"isStart":false})});
            var Q9;
            Q9=makeQuery(id+"F14.boolean.opBoolean","COPY",FACE,{"derivedFrom":makeQuery(id+"F14.opExtrude","CAP_FACE",FACE,{"disambiguationData":[OSD([sQuery(id+"F13.wireOp",EDGE,"E49.sketch_text.stroke-90"),sQuery(id+"F13.wireOp",EDGE,"E49.sketch_text.stroke-91"),sQuery(id+"F13.wireOp",EDGE,"E49.sketch_text.stroke-92"),sQuery(id+"F13.wireOp",EDGE,"E49.sketch_text.stroke-93")])],"isStart":false})});
            extrude(context, id + "F15", {"entities" : qUnion([Q0, Q1, Q2, Q3, Q4, Q5, Q6, Q7, Q8, Q9]), "depth" : 3 * mm, "offsetDistance" : 25 * mm});
        }
    });
